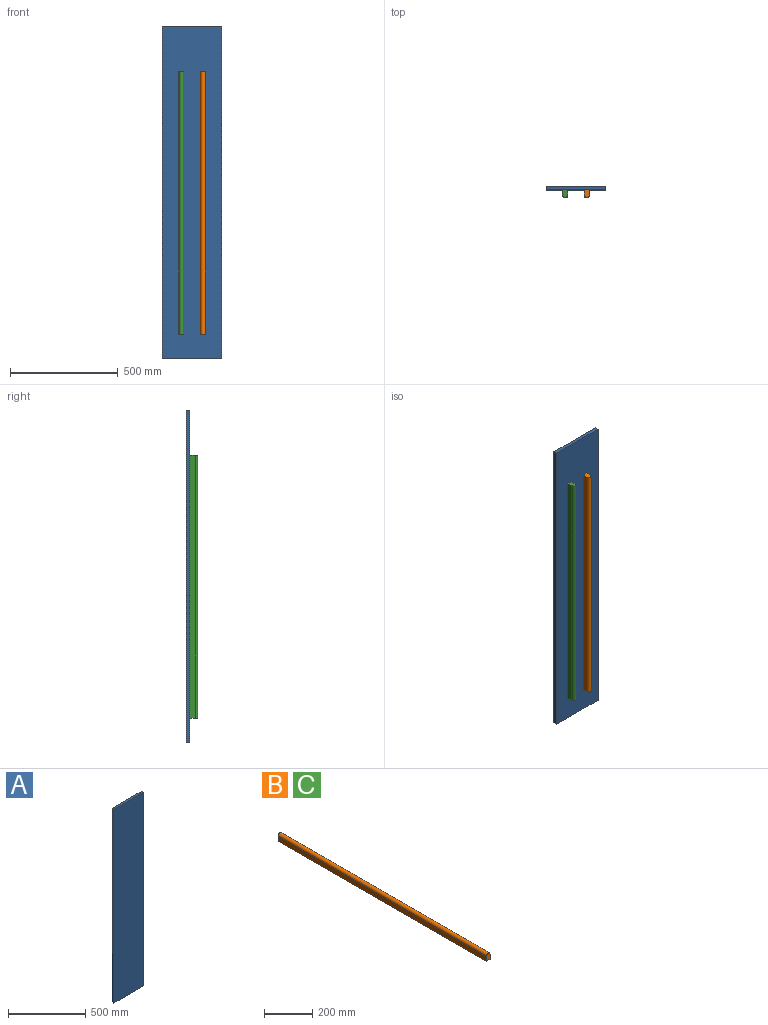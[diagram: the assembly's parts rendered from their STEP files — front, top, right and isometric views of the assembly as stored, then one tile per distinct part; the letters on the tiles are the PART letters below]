
ASSEMBLY  parts=3 mates=2
PART A: 6 faces, bbox 275x16x1540 mm
  f0: plane 275x16mm, normal (0,0,1), area 4400mm2, adj f1,f3,f4,f5
  f1: plane 1540x16mm, normal (-1,0,0), area 24640mm2, adj f0,f2,f4,f5
  f2: plane 275x16mm, normal (0,0,-1), area 4400mm2, adj f1,f3,f4,f5
  f3: plane 1540x16mm, normal (1,0,0), area 24640mm2, adj f0,f2,f4,f5
  f4: plane 1540x275mm, normal (0,-1,0), area 423500mm2, adj f0,f1,f2,f3
  f5: plane 1540x275mm, normal (0,1,0), area 423500mm2, adj f0,f1,f2,f3
PART B: 6 faces, bbox 22.4x1219.2x37.1 mm
  f0: plane 1219.2x25.9mm, normal (1,0,0), area 31577.3mm2, adj f1,f3,f4,f5
  f1: cylinder r=11.2mm len=1219.2mm, axis (0,1,0), area 42898.6mm2, adj f0,f2,f4,f5
  f2: plane 1219.2x25.9mm, normal (-1,0,0), area 31577.3mm2, adj f1,f3,f4,f5
  f3: plane 1219.2x22.4mm, normal (0,0,-1), area 27310.1mm2, adj f0,f2,f4,f5
  f4: plane 37.1x22.4mm, normal (0,-1,0), area 777.2mm2, adj f0,f1,f2,f3
  f5: plane 37.1x22.4mm, normal (0,1,0), area 777.2mm2, adj f0,f1,f2,f3
PART C: same geometry as B
PLACE A t=(-2080,0,-145)mm fixed
PLACE B rot(axis=(1,0,0),90deg) t=(502.5,-16,770)mm
PLACE C rot(axis=(1,0,0),90deg) t=(402.5,-16,770)mm
MATE fastened C.f3 <-> A.f4  axis (0,1,0) through (402.5,-16,770)mm
MATE fastened B.f3 <-> A.f4  axis (0,1,0) through (502.5,-16,770)mm
